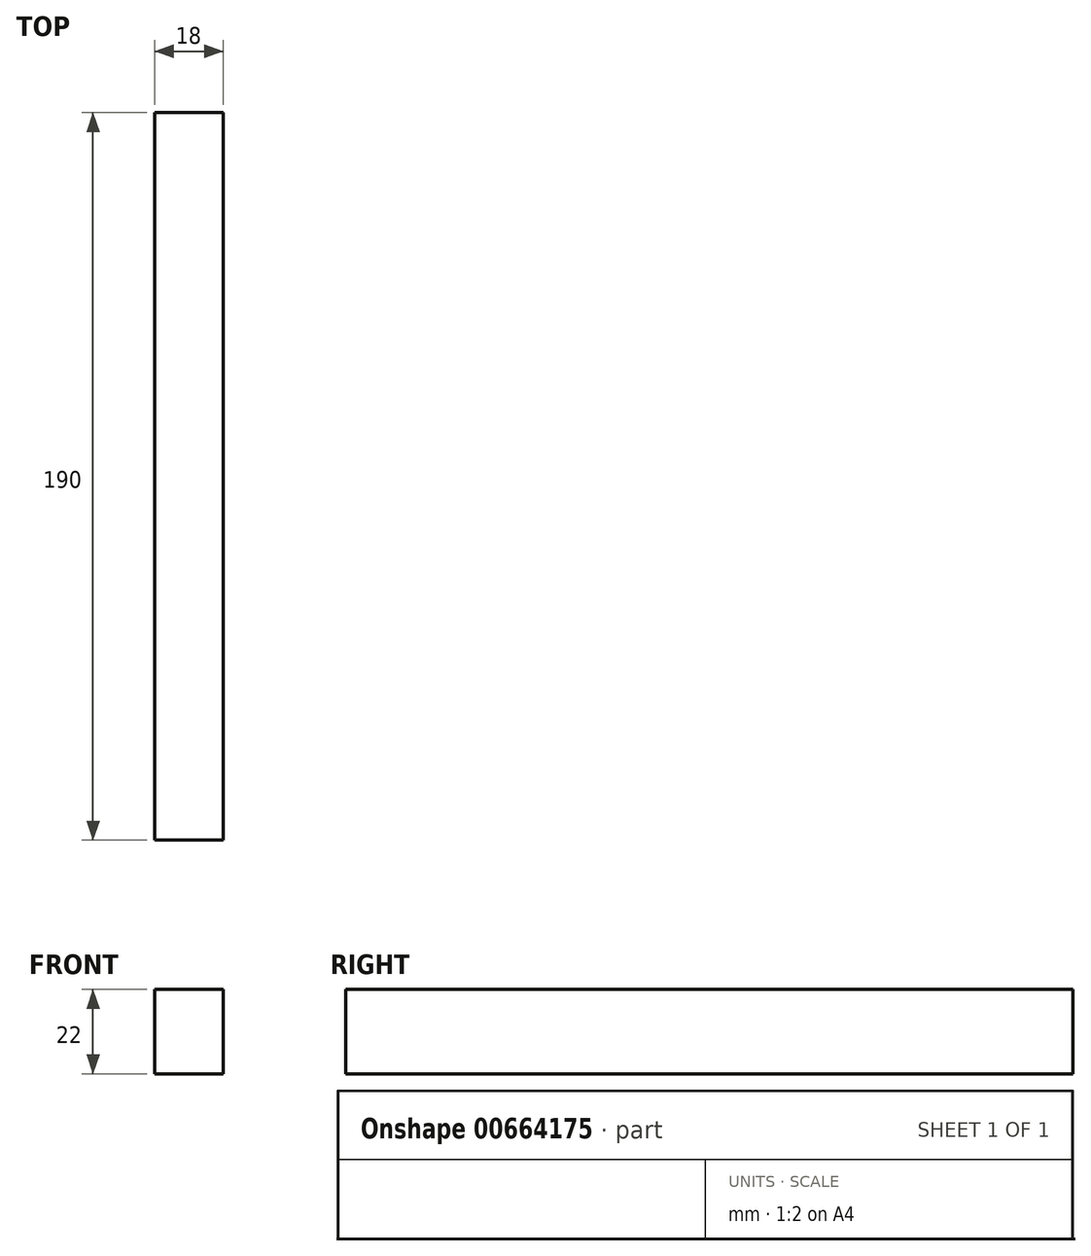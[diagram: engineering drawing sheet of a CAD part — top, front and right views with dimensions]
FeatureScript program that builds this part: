
annotation { "Feature Type Name" : "Feature", "Feature Type Description" : "" }
export const myFeature = defineFeature(function(context is Context, id is Id, definition is map)
    precondition{}
    {
        {
            var Q0;
            Q0=qCreatedBy(makeId("Top.planeOp"),FACE);
            var sketch = newSketch(context, id + "F0", { "sketchPlane" : qUnion([Q0])});
            skLineSegment(sketch, "E0.bottom", {"start": v(-9, 95) * mm, "end": v(9, 95) * mm});
            skLineSegment(sketch, "E0.top", {"start": v(-9, -95) * mm, "end": v(9, -95) * mm});
            skLineSegment(sketch, "E0.left", {"start": v(-9, 95) * mm, "end": v(-9, -95) * mm});
            skLineSegment(sketch, "E0.right", {"start": v(9, 95) * mm, "end": v(9, -95) * mm});
            skSolve(sketch);
        }
        {
            var Q0;
            Q0=makeQuery(id+"F0.imprint","IMPRINT",FACE,{"disambiguationData":[TD([[makeQuery(id+"F0.imprint","IMPRINT",EDGE,{"derivedFrom":sQuery(id+"F0.wireOp",EDGE,"E0.bottom")}),-1.0]])]});
            extrude(context, id + "F1", {"entities" : qUnion([Q0]), "depth" : 22 * mm, "offsetDistance" : 25 * mm});
        }
    });
